# Revit family: litepole_2___st1_2a_5xa5423er14h000032_bb05
name_source: partatom
category: Lighting Fixtures
units: mm (PartAtom-declared; Revit-internal decimal feet)

## family parameters
Cut with Voids When Loaded = No
Host = Face
Light Source = No
Part Type = Normal
Room Calculation Point = No
Round Connector Dimension = Use Diameter
Shared = No

## types (1)
- --- (1 x LED, 1550 lm, 14.2 W, 3000K)
    Apparent Load = 14 VA
    CIE Flux Codes = 22 60 92 98 100
    Color Rendering = 80
    Color Temperature = 3000K
    Default Elevation = 1800 mm
    Description = Litepole 2, mast luminaire, Module 540 Plus, primary light control with 3 zone facetted reflector, of plastic, silver coated, highly specular, structured, primary optical cover: cover, of PMMA, transparent, light distribution: ST1.2a, light emission: direct distribution, primary light characteristic: asymmetric, installation type: post-top, LED, High Power LED, rated luminous flux: 1.550lm, luminous efficacy: 109lm/W, light colour: 830, colour temperature: 3000K, control gear: ECG Smart Interface, control: overheat protection, digital communication interface, time-dependent luminous flux control, flexible luminous flux parameterisation, presetting dimming logarithmic, with terminal, 6-pole, max. 2.5mm², mains connection: 230..240V, AC, 50/60Hz, start of lifetime: 14W, end of service life: 15W, reduction: 8W, luminaire housing, upper part, of aluminium, coated, Siteco® metallic grey (DB 702S), diameter: 750mm, height: 590mm, spigot size: d x l = 76 x 70mm (post-top) | with reducer (optional accessory) 60 x 70mm, post-top mast mounting element, of diecast aluminium, coated, Siteco® metallic grey (DB 702S), Module 540 Plus, traffic white (RAL 9016), Smart Interface below, protection rating (complete): IP65, insulation class (complete): insulation class II (safety insulation), certification: CE, ENEC, VDE, packaging unit: 1 piece

Light Distribution: ST1.2a
    Height = 590 mm
    Lamp = 1 x LED
    Lamp Light Flux = 1550 lm
    Lamp Power = 14.2 W
    Lamp count = 1
    Length = 750 mm
    Luminous efficacy = 109 lm/W
    Manufacturer = Siteco
    ModVariant = No
    Model = 5XA5423ER14H000032
    Number of Poles = 1
    OnlyDefault = Yes
    Power Factor = 1
    Product Name = Litepole 2 | ST1.2a
    Product group = mast luminaire | pylon top
    ProductGroupID = 6100
    Protection Class = Protection class II
    Protection Degree = IP 65
    RLX_Detail_Level = 1
    RLX_Emergency_Light_Flux = 0 lm
    RLX_Emergency_Type = 0
    RLX_Emergency_Type_DB = No
    RlxData = <blob elided: 115429 chars, md5=7cae2851>
    Socket = socket
    Standby Power = 0 W
    System Light Flux = 1550 lm
    System Power = 14 W
    Type Comments = factory setting: luminous flux: 100 % | dim-lin: 254 | 516 mA
    Type Image = l_1006503.jpg
    URL = http://relux.com
    VarID = @adj_151243
    Voltage = 0 V
    Weight = 0.00 kg
    Width = 0 mm  [stored 0 ft]

note: [stored X ft] marks values corroborated as IEEE doubles in the binary element streams (Revit-internal decimal feet)

## geometry (parser evidence)
native form markers: Sweep x11
no freeform markers — native parametric forms only
